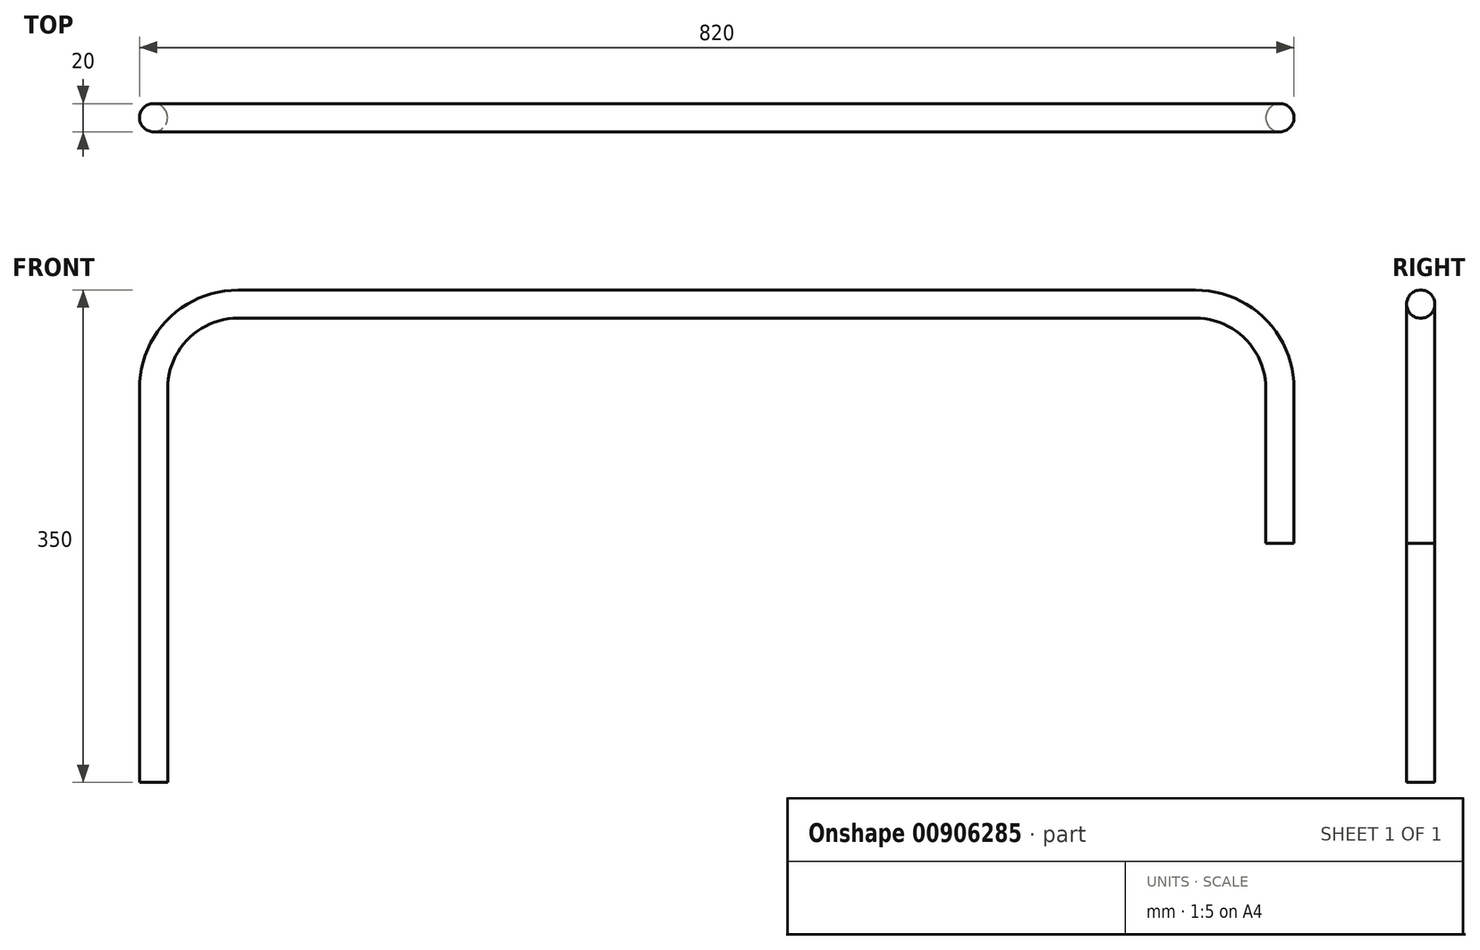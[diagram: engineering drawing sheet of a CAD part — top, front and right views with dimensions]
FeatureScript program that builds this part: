
annotation { "Feature Type Name" : "Feature", "Feature Type Description" : "" }
export const myFeature = defineFeature(function(context is Context, id is Id, definition is map)
    precondition{}
    {
        {
            var Q0;
            Q0=qCreatedBy(makeId("Front.planeOp"),FACE);
            var sketch = newSketch(context, id + "F0", { "sketchPlane" : qUnion([Q0])});
            skLineSegment(sketch, "E0", {"start": v(0, 0) * mm, "end": v(0, 110) * mm});
            skLineSegment(sketch, "E1", {"start": v(-60, 170) * mm, "end": v(-740, 170) * mm});
            skLineSegment(sketch, "E2", {"start": v(-800, 110) * mm, "end": v(-800, -170) * mm});
            skPoint(sketch, "E3.visualSharp", {"position": v(0, 170) * mm});
            skArc(sketch, "E3.filletArc", {"start": v(0, 110) * mm, "mid": v(-17.57, 152.43) * mm, "end": v(-60, 170) * mm});
            skPoint(sketch, "E4.visualSharp", {"position": v(-800, 170) * mm});
            skArc(sketch, "E4.filletArc", {"start": v(-740, 170) * mm, "mid": v(-782.43, 152.43) * mm, "end": v(-800, 110) * mm});
            skSolve(sketch);
        }
        {
            var Q0;
            Q0=qCreatedBy(makeId("Top.planeOp"),FACE);
            var sketch = newSketch(context, id + "F1", { "sketchPlane" : qUnion([Q0])});
            skCircle(sketch, "E5", {"center": v(0, 0) * mm, "radius": 10 * mm});
            skSolve(sketch);
        }
        {
            var Q0;
            Q0=makeQuery(id+"F1.imprint","IMPRINT",FACE,{"disambiguationData":[TD([[makeQuery(id+"F1.imprint","IMPRINT",EDGE,{"derivedFrom":sQuery(id+"F1.wireOp",EDGE,"E5")}),1.0]])]});
            var Q1;
            Q1=sQuery(id+"F0.wireOp",EDGE,"E1");
            var Q2;
            Q2=sQuery(id+"F0.wireOp",EDGE,"E3.filletArc");
            var Q3;
            Q3=sQuery(id+"F0.wireOp",EDGE,"E0");
            var Q4;
            Q4=sQuery(id+"F0.wireOp",EDGE,"E4.filletArc");
            var Q5;
            Q5=sQuery(id+"F0.wireOp",EDGE,"E2");
            sweep(context, id + "F2", {"profiles" : qUnion([Q0]), "path" : qUnion([Q1, Q2, Q3, Q4, Q5])});
        }
    });
